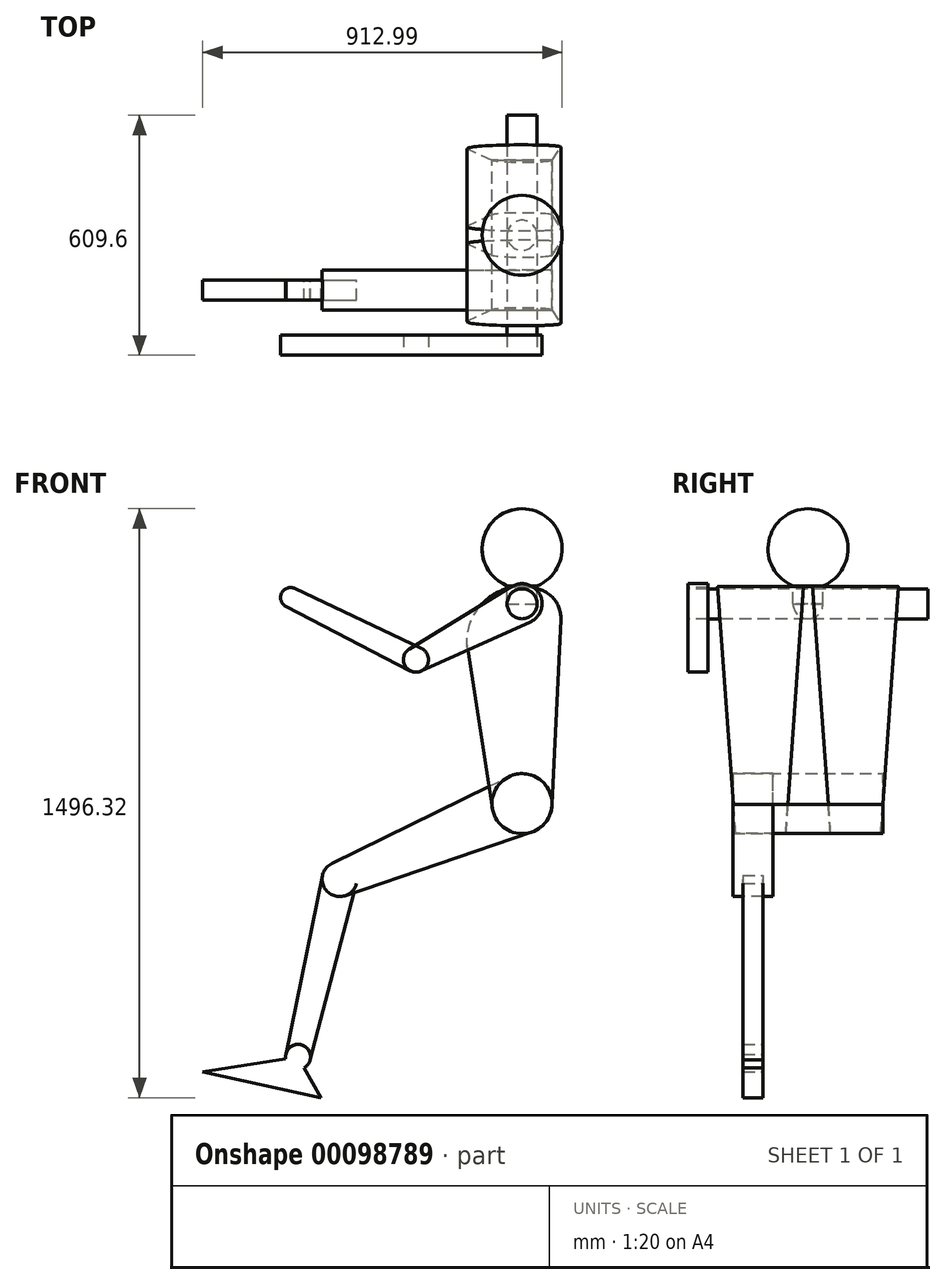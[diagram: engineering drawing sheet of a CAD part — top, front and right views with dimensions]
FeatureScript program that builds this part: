
annotation { "Feature Type Name" : "Feature", "Feature Type Description" : "" }
export const myFeature = defineFeature(function(context is Context, id is Id, definition is map)
    precondition{}
    {
        {
            var Q0;
            Q0=qCreatedBy(makeId("Front.planeOp"),FACE);
            var sketch = newSketch(context, id + "F0", { "sketchPlane" : qUnion([Q0])});
            skLineSegment(sketch, "E0", {"start": v(0, 0) * mm, "end": v(0, -241.3) * mm});
            skLineSegment(sketch, "E1", {"start": v(-33.7, -259.08) * mm, "end": v(-269.6, -383.5) * mm});
            skLineSegment(sketch, "E2", {"start": v(-269.6, -383.5) * mm, "end": v(-587.34, -223.85) * mm});
            skLineSegment(sketch, "E3", {"start": v(0, -241.3) * mm, "end": v(0, -749.3) * mm});
            skLineSegment(sketch, "E4", {"start": v(0, -749.3) * mm, "end": v(-463.54, -941.1) * mm});
            skLineSegment(sketch, "E5", {"start": v(-463.54, -941.1) * mm, "end": v(-561.6, -1394.16) * mm});
            skLineSegment(sketch, "E6", {"start": v(-803.83, -1432.69) * mm, "end": v(-504.78, -1497.41) * mm});
            skLineSegment(sketch, "E7", {"start": v(-803.83, -1432.69) * mm, "end": v(-561.6, -1394.16) * mm});
            skLineSegment(sketch, "E8", {"start": v(-561.6, -1394.16) * mm, "end": v(-504.78, -1497.41) * mm});
            skArc(sketch, "E9", {"start": v(-38.1, -240.6) * mm, "mid": v(-27.18, -268) * mm, "end": v(0, -279.4) * mm});
            skArc(sketch, "E10", {"start": v(0, 0) * mm, "mid": v(-99.73, -82.2) * mm, "end": v(-38.1, -195.79) * mm});
            skLineSegment(sketch, "E11", {"start": v(-38.1, -242) * mm, "end": v(-38.1, -195.79) * mm});
            skSolve(sketch);
        }
        {
            var Q0;
            Q0=qCreatedBy(makeId("Top.planeOp"),FACE);
            var sketch = newSketch(context, id + "F1", { "sketchPlane" : qUnion([Q0])});
            skCircle(sketch, "E12", {"center": v(0, 0) * mm, "radius": 121.35 * mm});
            skSolve(sketch);
        }
        {
            var Q0;
            {var subQ6=sQuery(id+"F0.wireOp",EDGE,"E0");Q0=makeQuery(id+"F0.imprint","IMPRINT",FACE,{"disambiguationData":[TD([[makeQuery(id+"F0.imprint","IMPRINT",EDGE,{"derivedFrom":subQ6}),-1.0]])]});}
            var Q1;
            Q1=sQuery(id+"F1.wireOp",EDGE,"E12");
            sweep(context, id + "F2", {"profiles" : qUnion([Q0]), "path" : qUnion([Q1])});
        }
        {
            var Q0;
            Q0=qCreatedBy(makeId("Front.planeOp"),FACE);
            cPlane(context, id + "F3", {"entities" : qUnion([Q0]), "cplaneType" : CPlaneType.OFFSET, "offset" : 304.8 * mm, "width" : 152.4 * mm, "height" : 152.4 * mm});
        }
        {
            var Q0;
            Q0=qCreatedBy(id+"F3.planeOp",FACE);
            var sketch = newSketch(context, id + "F4", { "sketchPlane" : qUnion([Q0])});
            skArc(sketch, "E13", {"start": v(20.85, -287.63) * mm, "mid": v(44.93, -217.6) * mm, "end": v(-26.46, -197.94) * mm});
            skLineSegment(sketch, "E14", {"start": v(-287.24, -357.07) * mm, "end": v(0, -181.79) * mm});
            skLineSegment(sketch, "E15", {"start": v(-257.12, -412.7) * mm, "end": v(20.85, -287.63) * mm});
            skLineSegment(sketch, "E16", {"start": v(-269.6, -383.5) * mm, "end": v(0, -241.3) * mm});
            skArc(sketch, "E17", {"start": v(-286.13, -356.4) * mm, "mid": v(-297.68, -398.32) * mm, "end": v(-256.57, -412.46) * mm});
            skSolve(sketch);
        }
        {
            var Q0;
            Q0 = qSketchRegion(id + "F4", true);
            extrude(context, id + "F5", {"entities" : qUnion([Q0]), "oppositeDirection" : true, "depth" : 50.8 * mm});
        }
        {
            var Q0;
            {var subQ0=sQuery(id+"F4.wireOp",EDGE,"E13");Q0=makeQuery(id+"F4.imprint","IMPRINT",FACE,{"disambiguationData":[TD([[makeQuery(id+"F4.imprint","IMPRINT",EDGE,{"derivedFrom":subQ0}),1.0]])]});}
            var sketch = newSketch(context, id + "F6", { "sketchPlane" : qUnion([Q0])});
            skCircle(sketch, "E18", {"center": v(0, -241.54) * mm, "radius": 38.1 * mm});
            skSolve(sketch);
        }
        {
            var Q0;
            {var subQ0=sQuery(id+"F6.wireOp",EDGE,"E18");var subQ1=sQuery(id+"F4.wireOp",EDGE,"E13");var subQ2=makeQuery(id+"F4.imprint","IMPRINT",EDGE,{"derivedFrom":subQ1});var subQ3=makeQuery(id+"F6.imprint","INTERSECT",VERTEX,{"derivedFrom":[subQ2,subQ0]});Q0=makeQuery(id+"F6.imprint","IMPRINT",FACE,{"disambiguationData":[TD([[makeQuery(id+"F6.imprint","IMPRINT",EDGE,{"disambiguationData":[TD([[subQ3,-1.0]])],"derivedFrom":subQ0}),1.0]])]});}
            var sketch = newSketch(context, id + "F7", { "sketchPlane" : qUnion([Q0])});
            skCircle(sketch, "E19", {"center": v(0, -241.54) * mm, "radius": 38.1 * mm});
            skSolve(sketch);
        }
        {
            var Q0;
            Q0 = qSketchRegion(id + "F7", true);
            extrude(context, id + "F8", {"entities" : qUnion([Q0]), "oppositeDirection" : true, "depth" : 609.6 * mm});
        }
        {
            var Q0;
            Q0=qCreatedBy(id+"F3.planeOp",FACE);
            var sketch = newSketch(context, id + "F9", { "sketchPlane" : qUnion([Q0])});
            skLineSegment(sketch, "E20", {"start": v(-269.6, -383.5) * mm, "end": v(-588.3, -225.75) * mm});
            skCircle(sketch, "E21", {"center": v(-588.3, -225.75) * mm, "radius": 25.4 * mm});
            skCircle(sketch, "E22", {"center": v(-269.6, -383.5) * mm, "radius": 31.75 * mm});
            skLineSegment(sketch, "E23", {"start": v(-577.43, -202.8) * mm, "end": v(-256.02, -354.8) * mm});
            skLineSegment(sketch, "E24", {"start": v(-599.96, -248.31) * mm, "end": v(-284.19, -411.7) * mm});
            skSolve(sketch);
        }
        {
            var Q0;
            Q0 = qSketchRegion(id + "F9", true);
            extrude(context, id + "F10", {"entities" : qUnion([Q0]), "oppositeDirection" : true, "depth" : 50.8 * mm});
        }
        {
            var Q0;
            Q0=qCreatedBy(makeId("Front.planeOp"),FACE);
            cPlane(context, id + "F11", {"entities" : qUnion([Q0]), "cplaneType" : CPlaneType.OFFSET, "offset" : 190.5 * mm, "width" : 152.4 * mm, "height" : 152.4 * mm});
        }
        {
            var Q0;
            Q0=qCreatedBy(id+"F11.planeOp",FACE);
            var sketch = newSketch(context, id + "F12", { "sketchPlane" : qUnion([Q0])});
            skArc(sketch, "E25", {"start": v(24.62, -821.41) * mm, "mid": v(70.41, -720.17) * mm, "end": v(-33.53, -680.87) * mm});
            skArc(sketch, "E26", {"start": v(-483.1, -901.18) * mm, "mid": v(-504.61, -958.1) * mm, "end": v(-449.18, -983.16) * mm});
            skLineSegment(sketch, "E27", {"start": v(-483.1, -901.18) * mm, "end": v(-33.53, -680.87) * mm});
            skLineSegment(sketch, "E28", {"start": v(-449.18, -983.16) * mm, "end": v(24.62, -821.41) * mm});
            skSolve(sketch);
        }
        {
            var Q0;
            Q0 = qSketchRegion(id + "F12", true);
            extrude(context, id + "F13", {"entities" : qUnion([Q0]), "oppositeDirection" : true, "depth" : 101.6 * mm});
        }
        {
            var Q0;
            Q0=makeQuery(id+"F13.opExtrude","CAP_FACE",FACE,{"disambiguationData":[OSD([sQuery(id+"F12.wireOp",EDGE,"E25"),sQuery(id+"F12.wireOp",EDGE,"E26"),sQuery(id+"F12.wireOp",EDGE,"E27"),sQuery(id+"F12.wireOp",EDGE,"E28")])],"isStart":true});
            cPlane(context, id + "F14", {"entities" : qUnion([Q0]), "cplaneType" : CPlaneType.OFFSET, "offset" : 50.8 * mm, "oppositeDirection" : true, "width" : 152.4 * mm, "height" : 152.4 * mm});
        }
        {
            var Q0;
            Q0=qCreatedBy(id+"F14.planeOp",FACE);
            var sketch = newSketch(context, id + "F15", { "sketchPlane" : qUnion([Q0])});
            skCircle(sketch, "E29", {"center": v(-463.54, -941.1) * mm, "radius": 44.45 * mm});
            skCircle(sketch, "E30", {"center": v(-569.15, -1392.75) * mm, "radius": 31.75 * mm});
            skLineSegment(sketch, "E31", {"start": v(-600.26, -1386.37) * mm, "end": v(-507.08, -932.16) * mm});
            skLineSegment(sketch, "E32", {"start": v(-538.45, -1400.82) * mm, "end": v(-420.55, -952.4) * mm});
            skSolve(sketch);
        }
        {
            var Q0;
            {var subQ0=sQuery(id+"F15.wireOp",EDGE,"E31");Q0=makeQuery(id+"F15.imprint","IMPRINT",FACE,{"disambiguationData":[TD([[makeQuery(id+"F15.imprint","IMPRINT",EDGE,{"derivedFrom":subQ0}),-1.0]])]});}
            extrude(context, id + "F16", {"entities" : qUnion([Q0]), "depth" : 50.8 * mm, "symmetric" : true});
        }
        {
            var Q0;
            Q0=qCreatedBy(id+"F14.planeOp",FACE);
            var sketch = newSketch(context, id + "F17", { "sketchPlane" : qUnion([Q0])});
            skLineSegment(sketch, "E33", {"start": v(-575.87, -1423.78) * mm, "end": v(-575.87, -1423.78) * mm});
            skLineSegment(sketch, "E34", {"start": v(-587.96, -1479.64) * mm, "end": v(-510.86, -1496.32) * mm});
            skLineSegment(sketch, "E35", {"start": v(-587.96, -1479.64) * mm, "end": v(-811.39, -1431.28) * mm});
            skLineSegment(sketch, "E36", {"start": v(-811.39, -1431.28) * mm, "end": v(-600.5, -1397.74) * mm});
            skLineSegment(sketch, "E37", {"start": v(-510.86, -1496.32) * mm, "end": v(-553.58, -1420.42) * mm});
            skArc(sketch, "E38.trimOffspring", {"start": v(-553.58, -1420.42) * mm, "mid": v(-555.34, -1364.16) * mm, "end": v(-600.5, -1397.74) * mm});
            skSolve(sketch);
        }
        {
            var Q0;
            Q0 = qSketchRegion(id + "F17", true);
            extrude(context, id + "F18", {"entities" : qUnion([Q0]), "depth" : 50.8 * mm, "symmetric" : true});
        }
        {
            var Q0;
            Q0=qCreatedBy(makeId("Right.planeOp"),FACE);
            var sketch = newSketch(context, id + "F19", { "sketchPlane" : qUnion([Q0])});
            skLineSegment(sketch, "E39", {"start": v(-227.12, -234.95) * mm, "end": v(-190.5, -742.95) * mm});
            skSolve(sketch);
        }
        {
            var Q0;
            Q0=sQuery(id+"F19.wireOp",EDGE,"E39");
            cPlane(context, id + "F20", {"entities" : qUnion([Q0]), "cplaneType" : CPlaneType.LINE_ANGLE, "offset" : 152.4 * mm, "angle" : 90 * degree, "width" : 152.4 * mm, "height" : 152.4 * mm});
        }
        {
            var Q0;
            Q0=qCreatedBy(id+"F20.planeOp",FACE);
            var sketch = newSketch(context, id + "F21", { "sketchPlane" : qUnion([Q0])});
            skArc(sketch, "E40", {"start": v(138.04, -341.74) * mm, "mid": v(88.24, -211.98) * mm, "end": v(-48.92, -189.43) * mm});
            skArc(sketch, "E41", {"start": v(-76.18, -735.61) * mm, "mid": v(-4.95, -809.8) * mm, "end": v(75.3, -745.47) * mm});
            skLineSegment(sketch, "E42", {"start": v(75.3, -745.47) * mm, "end": v(138.04, -341.74) * mm});
            skLineSegment(sketch, "E43", {"start": v(-76.18, -735.61) * mm, "end": v(-98.35, -264.39) * mm});
            skArc(sketch, "E44", {"start": v(-48.92, -189.43) * mm, "mid": v(-85.85, -218.86) * mm, "end": v(-98.35, -264.39) * mm});
            skPoint(sketch, "E45.orphan", {"position": v(-101.6, -195.33) * mm});
            skSolve(sketch);
        }
        {
            var Q0;
            Q0=qCreatedBy(makeId("Right.planeOp"),FACE);
            var sketch = newSketch(context, id + "F22", { "sketchPlane" : qUnion([Q0])});
            skLineSegment(sketch, "E46", {"start": v(50.8, -621.45) * mm, "end": v(-190.5, -621.45) * mm});
            skSolve(sketch);
        }
        {
            var Q0;
            Q0=makeQuery(id+"F21.imprint","IMPRINT",FACE,{"disambiguationData":[TD([[makeQuery(id+"F21.imprint","IMPRINT",EDGE,{"derivedFrom":sQuery(id+"F21.wireOp",EDGE,"E40")}),1.0]])]});
            var Q1;
            Q1=sQuery(id+"F22.wireOp",EDGE,"E46");
            sweep(context, id + "F23", {"profiles" : qUnion([Q0]), "path" : qUnion([Q1])});
        }
        {
            var Q0;
            Q0=makeQuery(id+"F23.opSweep","SWEPT_BODY",BODY,{"disambiguationData":[OSD([sQuery(id+"F21.wireOp",EDGE,"E40"),sQuery(id+"F21.wireOp",EDGE,"E41"),sQuery(id+"F21.wireOp",EDGE,"E42"),sQuery(id+"F21.wireOp",EDGE,"E43"),sQuery(id+"F21.wireOp",EDGE,"E44"),sQuery(id+"F22.wireOp",EDGE,"E46")])]});
            var Q1;
            Q1=qCreatedBy(makeId("Front.planeOp"),FACE);
            mirror(context, id + "F24", {"entities" : qUnion([Q0]), "mirrorPlane" : qUnion([Q1])});
        }
        {
            var Q0;
            Q0=qCreatedBy(makeId("Front.planeOp"),FACE);
            var sketch = newSketch(context, id + "F25", { "sketchPlane" : qUnion([Q0])});
            skCircle(sketch, "E47", {"center": v(0, -749.3) * mm, "radius": 76.2 * mm});
            skSolve(sketch);
        }
        {
            var Q0;
            Q0 = qSketchRegion(id + "F25", true);
            extrude(context, id + "F26", {"entities" : qUnion([Q0]), "depth" : 381 * mm, "symmetric" : true});
        }
    });
